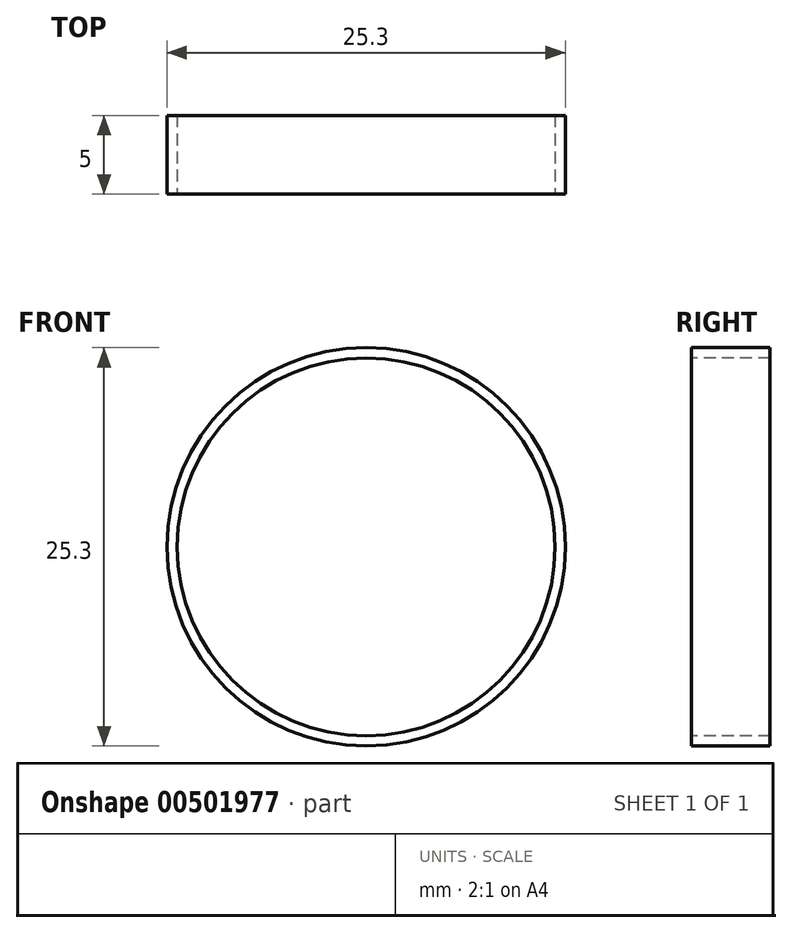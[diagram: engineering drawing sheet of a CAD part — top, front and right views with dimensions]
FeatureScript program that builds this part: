
annotation { "Feature Type Name" : "Feature", "Feature Type Description" : "" }
export const myFeature = defineFeature(function(context is Context, id is Id, definition is map)
    precondition{}
    {
        {
            var Q0;
            Q0=qCreatedBy(makeId("Front.planeOp"),FACE);
            var sketch = newSketch(context, id + "F0", { "sketchPlane" : qUnion([Q0])});
            skCircle(sketch, "E0", {"center": v(0, 0) * mm, "radius": 12 * mm});
            skCircle(sketch, "E1", {"center": v(0, 0) * mm, "radius": 12.65 * mm});
            skSolve(sketch);
        }
        {
            var Q0;
            Q0=sQuery(id+"F0.wireOp",EDGE,"E0");
            var Q1;
            Q1=sQuery(id+"F0.wireOp",EDGE,"E1");
            extrude(context, id + "F1", {"bodyType" : ToolBodyType.SURFACE, "surfaceEntities" : qUnion([Q0, Q1]), "depth" : 5 * mm});
        }
    });
